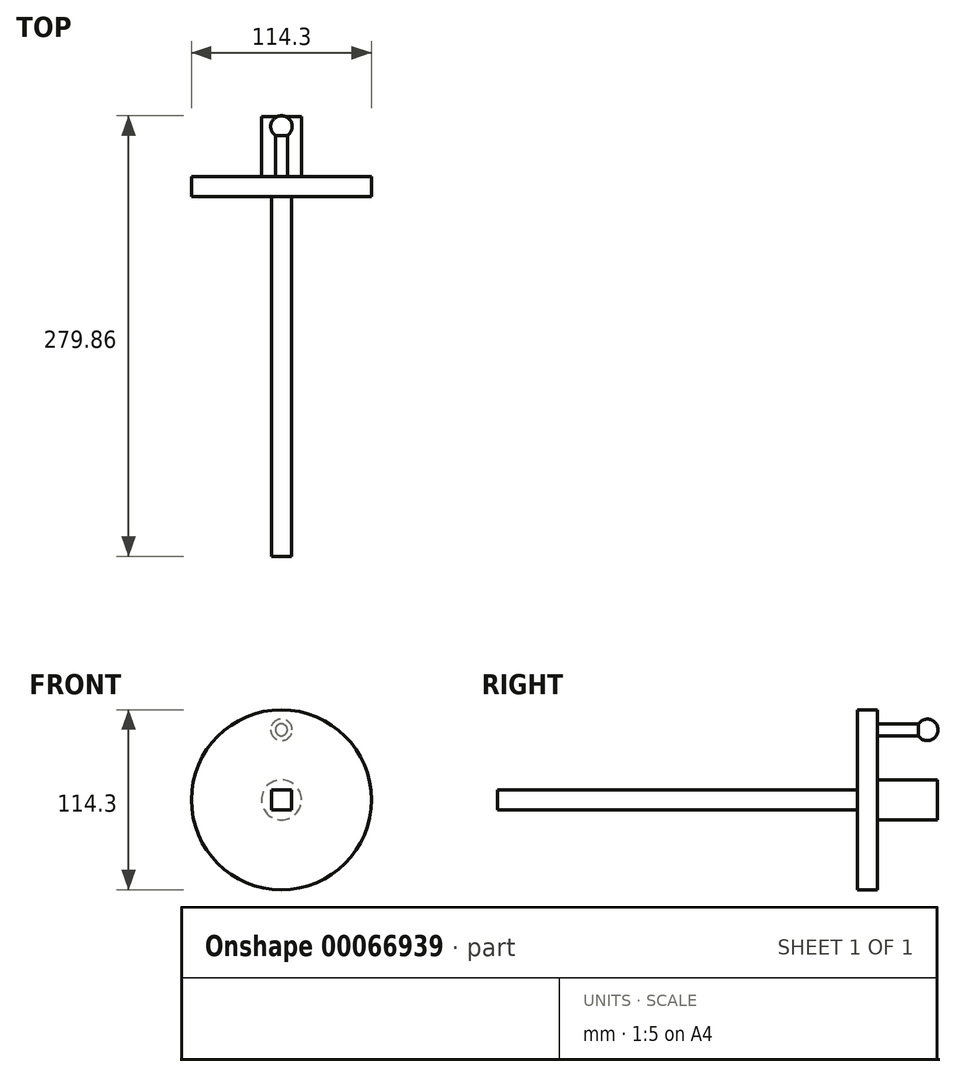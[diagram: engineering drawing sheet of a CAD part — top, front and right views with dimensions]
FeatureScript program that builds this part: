
annotation { "Feature Type Name" : "Feature", "Feature Type Description" : "" }
export const myFeature = defineFeature(function(context is Context, id is Id, definition is map)
    precondition{}
    {
        {
            var Q0;
            Q0=qCreatedBy(makeId("Front.planeOp"),FACE);
            var sketch = newSketch(context, id + "F0", { "sketchPlane" : qUnion([Q0])});
            skCircle(sketch, "E0", {"center": v(0, 0) * mm, "radius": 57.15 * mm});
            skSolve(sketch);
        }
        {
            var Q0;
            Q0=qSketchRegion(id+"F0",true);
            extrude(context, id + "F1", {"entities" : qUnion([Q0]), "depth" : 12.7 * mm});
        }
        {
            var Q0;
            Q0=makeQuery(id+"F1.opExtrude","CAP_FACE",FACE,{"disambiguationData":[OSD([sQuery(id+"F0.wireOp",EDGE,"E0")])],"isStart":false});
            var sketch = newSketch(context, id + "F2", { "sketchPlane" : qUnion([Q0])});
            skLineSegment(sketch, "E1.rect.bottom", {"start": v(6.35, 6.35) * mm, "end": v(-6.35, 6.35) * mm});
            skLineSegment(sketch, "E1.rect.top", {"start": v(6.35, -6.35) * mm, "end": v(-6.35, -6.35) * mm});
            skLineSegment(sketch, "E1.rect.left", {"start": v(6.35, 6.35) * mm, "end": v(6.35, -6.35) * mm});
            skLineSegment(sketch, "E1.rect.right", {"start": v(-6.35, 6.35) * mm, "end": v(-6.35, -6.35) * mm});
            skPoint(sketch, "E1.rect.middle", {"position": v(0, 0) * mm});
            skSolve(sketch);
        }
        {
            var Q0;
            Q0=qSketchRegion(id+"F2",true);
            extrude(context, id + "F3", {"entities" : qUnion([Q0]), "operationType" : NewBodyOperationType.ADD, "depth" : 228.6 * mm});
        }
        {
            var Q0;
            Q0=makeQuery(id+"F1.opExtrude","CAP_FACE",FACE,{"disambiguationData":[OSD([sQuery(id+"F0.wireOp",EDGE,"E0")])],"isStart":true});
            var sketch = newSketch(context, id + "F4", { "sketchPlane" : qUnion([Q0])});
            skCircle(sketch, "E2", {"center": v(0, 0) * mm, "radius": 12.7 * mm});
            skSolve(sketch);
        }
        {
            var Q0;
            Q0=qSketchRegion(id+"F4",true);
            extrude(context, id + "F5", {"entities" : qUnion([Q0]), "operationType" : NewBodyOperationType.ADD, "depth" : 38.1 * mm});
        }
        {
            var Q0;
            Q0=makeQuery(id+"F1.opExtrude","CAP_FACE",FACE,{"disambiguationData":[OSD([sQuery(id+"F0.wireOp",EDGE,"E0")])],"isStart":true});
            var sketch = newSketch(context, id + "F6", { "sketchPlane" : qUnion([Q0])});
            skCircle(sketch, "E3", {"center": v(0, 44.45) * mm, "radius": 3.81 * mm});
            skSolve(sketch);
        }
        {
            var Q0;
            Q0=makeQuery(id+"F6.imprint","IMPRINT",FACE,{"disambiguationData":[TD([[makeQuery(id+"F6.imprint","IMPRINT",EDGE,{"derivedFrom":sQuery(id+"F6.wireOp",EDGE,"E3")}),1.0]])]});
            extrude(context, id + "F7", {"entities" : qUnion([Q0]), "operationType" : NewBodyOperationType.ADD, "depth" : 31.75 * mm});
        }
        {
            var Q0;
            Q0=makeQuery(id+"F7.opExtrude","CAP_FACE",FACE,{"disambiguationData":[OSD([sQuery(id+"F6.wireOp",EDGE,"E3")])],"isStart":false});
            var sketch = newSketch(context, id + "F8", { "sketchPlane" : qUnion([Q0])});
            skLineSegment(sketch, "E4", {"start": v(-6.81, 44.45) * mm, "end": v(6.81, 44.45) * mm});
            skArc(sketch, "E5", {"start": v(6.81, 44.45) * mm, "mid": v(0, 51.26) * mm, "end": v(-6.81, 44.45) * mm});
            skLineSegment(sketch, "E6", {"start": v(0, 44.45) * mm, "end": v(-31.03, 44.45) * mm, "construction": true});
            skSolve(sketch);
        }
        {
            var Q0;
            {var subQ0=sQuery(id+"F8.wireOp",EDGE,"E5");Q0=makeQuery(id+"F8.imprint","IMPRINT",FACE,{"disambiguationData":[TD([[makeQuery(id+"F8.imprint","IMPRINT",EDGE,{"derivedFrom":subQ0}),1.0]])]});}
            var Q1;
            {var subQ0=sQuery(id+"F8.wireOp",EDGE,"E4");var subQ1=makeQuery(id+"F7.opExtrude","CAP_EDGE",EDGE,{"disambiguationData":[OSD([sQuery(id+"F6.wireOp",EDGE,"E3")])],"isStart":false});var subQ2=makeQuery(id+"F8.imprint","INTERSECT",VERTEX,{"disambiguationData":[OD(0.0)],"derivedFrom":[subQ1,subQ0]});Q1=makeQuery(id+"F8.imprint","IMPRINT",FACE,{"disambiguationData":[TD([[makeQuery(id+"F8.imprint","IMPRINT",EDGE,{"disambiguationData":[TD([[subQ2,-1.0]])],"derivedFrom":subQ0}),1.0]])]});}
            var Q2;
            Q2=sQuery(id+"F8.wireOp",EDGE,"E6");
            revolve(context, id + "F9", {"operationType" : NewBodyOperationType.ADD, "entities" : qUnion([Q0, Q1]), "axis" : qUnion([Q2]), "revolveType" : RevolveType.FULL});
        }
    });
